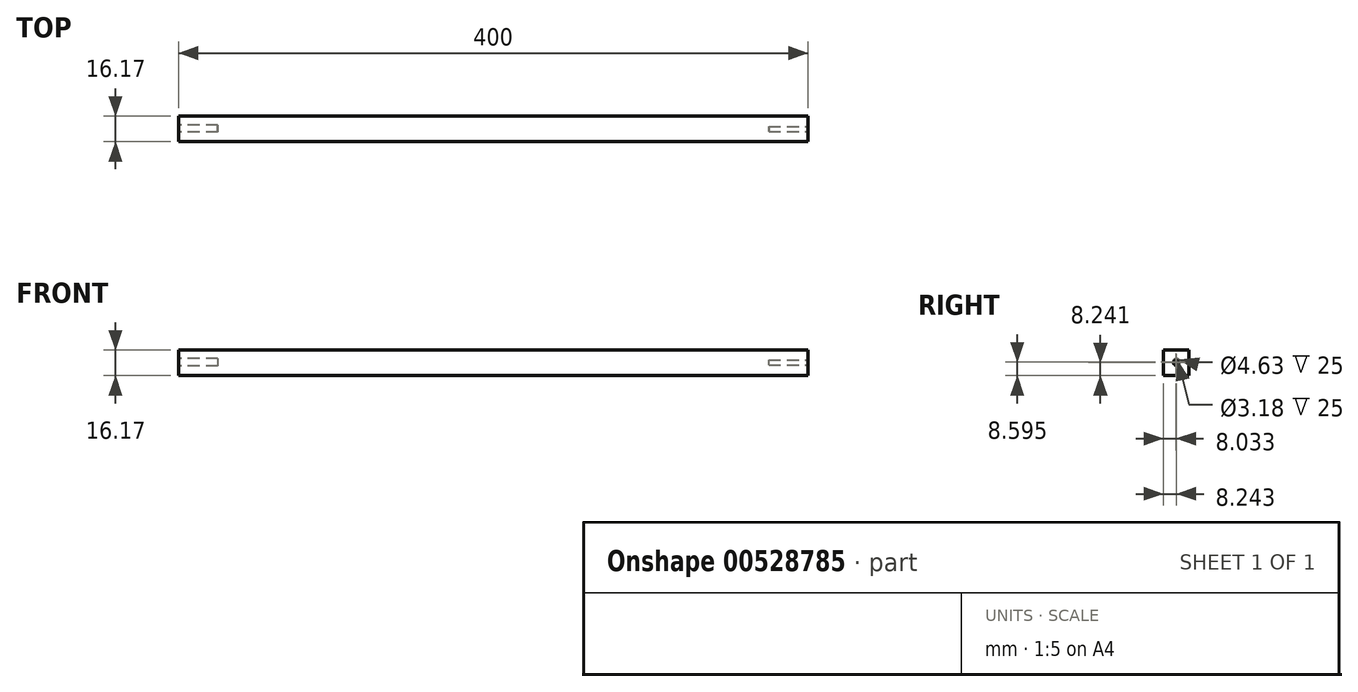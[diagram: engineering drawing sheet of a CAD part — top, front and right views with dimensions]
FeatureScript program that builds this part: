
annotation { "Feature Type Name" : "Feature", "Feature Type Description" : "" }
export const myFeature = defineFeature(function(context is Context, id is Id, definition is map)
    precondition{}
    {
        {
            var Q0;
            Q0=qCreatedBy(makeId("Right.planeOp"),FACE);
            var sketch = newSketch(context, id + "F0", { "sketchPlane" : qUnion([Q0])});
            skLineSegment(sketch, "E0.bottom", {"start": v(0, 0) * mm, "end": v(16.17, 0) * mm});
            skLineSegment(sketch, "E0.top", {"start": v(0, 16.17) * mm, "end": v(16.17, 16.17) * mm});
            skLineSegment(sketch, "E0.left", {"start": v(0, 0) * mm, "end": v(0, 16.17) * mm});
            skLineSegment(sketch, "E0.right", {"start": v(16.17, 0) * mm, "end": v(16.17, 16.17) * mm});
            skSolve(sketch);
        }
        {
            var Q0;
            Q0=makeQuery(id+"F0.imprint","IMPRINT",FACE,{"disambiguationData":[TD([[makeQuery(id+"F0.imprint","IMPRINT",EDGE,{"derivedFrom":sQuery(id+"F0.wireOp",EDGE,"E0.bottom")}),1.0]])]});
            extrude(context, id + "F1", {"entities" : qUnion([Q0]), "depth" : 400 * mm, "offsetDistance" : 25 * mm});
        }
        {
            var Q0;
            Q0=makeQuery(id+"F1.opExtrude","CAP_FACE",FACE,{"disambiguationData":[OSD([sQuery(id+"F0.wireOp",EDGE,"E0.bottom"),sQuery(id+"F0.wireOp",EDGE,"E0.top"),sQuery(id+"F0.wireOp",EDGE,"E0.left"),sQuery(id+"F0.wireOp",EDGE,"E0.right")])],"isStart":true});
            var sketch = newSketch(context, id + "F2", { "sketchPlane" : qUnion([Q0])});
            skCircle(sketch, "E1", {"center": v(-8.24, 8.6) * mm, "radius": 2.32 * mm});
            skSolve(sketch);
        }
        {
            var Q0;
            Q0=makeQuery(id+"F2.imprint","IMPRINT",FACE,{"disambiguationData":[TD([[makeQuery(id+"F2.imprint","IMPRINT",EDGE,{"derivedFrom":sQuery(id+"F2.wireOp",EDGE,"E1")}),1.0]])]});
            extrude(context, id + "F3", {"entities" : qUnion([Q0]), "operationType" : NewBodyOperationType.REMOVE, "oppositeDirection" : true, "depth" : 25 * mm, "offsetDistance" : 25 * mm});
        }
        {
            var Q0;
            Q0=makeQuery(id+"F1.opExtrude","CAP_FACE",FACE,{"disambiguationData":[OSD([sQuery(id+"F0.wireOp",EDGE,"E0.bottom"),sQuery(id+"F0.wireOp",EDGE,"E0.top"),sQuery(id+"F0.wireOp",EDGE,"E0.left"),sQuery(id+"F0.wireOp",EDGE,"E0.right")])],"isStart":false});
            var sketch = newSketch(context, id + "F4", { "sketchPlane" : qUnion([Q0])});
            skCircle(sketch, "E2", {"center": v(8.03, 8.24) * mm, "radius": 1.6 * mm});
            skSolve(sketch);
        }
        {
            var Q0;
            Q0 = qSketchRegion(id + "F4", true);
            extrude(context, id + "F5", {"entities" : qUnion([Q0]), "operationType" : NewBodyOperationType.REMOVE, "oppositeDirection" : true, "depth" : 25 * mm, "offsetDistance" : 25 * mm});
        }
    });
